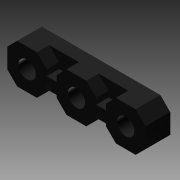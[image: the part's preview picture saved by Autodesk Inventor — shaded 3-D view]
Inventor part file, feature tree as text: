
AUTODESK INVENTOR PART (.ipt)
format: ipt  version: 2013 (Build 170138000, 138)  size: 224,768 bytes
history: native  units: mm (DEFAULTED — no unit token found)
features: extrude x7, sketch x6, other x3, chamfer x1, hole x1, pattern_linear x1
ambient origin geometry x8: Origin, YZ Plane, XZ Plane, XY Plane, X Axis, Y Axis, Z Axis, Center Point
bodies: Solid1 (feature_tree)
feature tree (19):
  extrude  "Extrusion1"  Depth=35.56mm
  chamfer  "Chamfer1"  Distance=3.175mm
  extrude  "Extrusion2"  Depth=10.16mm
  extrude  "Extrusion3"  Depth=2.54mm
  hole  "Hole1"  [1 undecoded]
  extrude  "Extrusion4"  Depth=2.54mm
  pattern_linear  "Rectangular Pattern1"  Spacing1=2.54mm  [1 undecoded]
  sketch  "Sketch1"  dims[d0=10.16mm d1=35.56mm d2=3.175mm d3=0.0mm]
  sketch  "Sketch2"  dims[d4=2.54mm d5=3.175mm d6=45.0deg d7=10.16mm]
  sketch  "Sketch3"  dims[d8=2.54mm d9=2.54mm]
  sketch  "Sketch4"  dims[d10=10.16mm d11=2.54mm]
  sketch  "Sketch5"  dims[d12=2.54mm d13=2.54mm]
  sketch  "Sketch6"  dims[d14=2.54mm d15=2.54mm d16=10.16mm d17=2.54mm d18=2.54mm d19=2.032mm d20=4.064mm d21=3.175mm d22=0.0mm d23=5.08mm d24=5.08mm d25=5.08mm d26=5.08mm d27=5.08mm d28=5.08mm d29=4.191mm d30=4.191mm d31=4.191mm d32=4.191mm d33=2.0955mm d34=2.0955mm d35=2.0955mm d36=2.0955mm d37=6.985mm d38=0.0mm d39=5.08mm d40=5.08mm d41=12.7mm d42=12.7mm d43=5.08mm d44=5.08mm d45=4.445mm d46=12.7mm d47=9.525mm d48=6.35mm d49=14.3117mm d50=19.05mm d51=20.594885mm d52=7.62mm d53=7.62mm d54=7.62mm d55=6.35mm d56=1.524mm d57=1.524mm d58=1.905mm d59=0.0mm d60=25.4mm d61=0.0mm d62=30.0mm d64=12.7mm d65=0.0mm d66=0.0mm d67=0.0mm d68=0.0mm d69=0.0mm d70=0.0mm]
  other  "Srf1"
  other  "Srf2"
  other  "Srf3"
  extrude  "ExtrusionSrf1"  Depth=10.16mm
  extrude  "ExtrusionSrf2"  Depth=2.54mm
  extrude  "ExtrusionSrf3"  Depth=2.54mm
note: 2 required parameter values undecoded (feature->parameter linkage not recoverable at this tier; creation-order binding heuristic only, values carry confidence <= 0.55)
